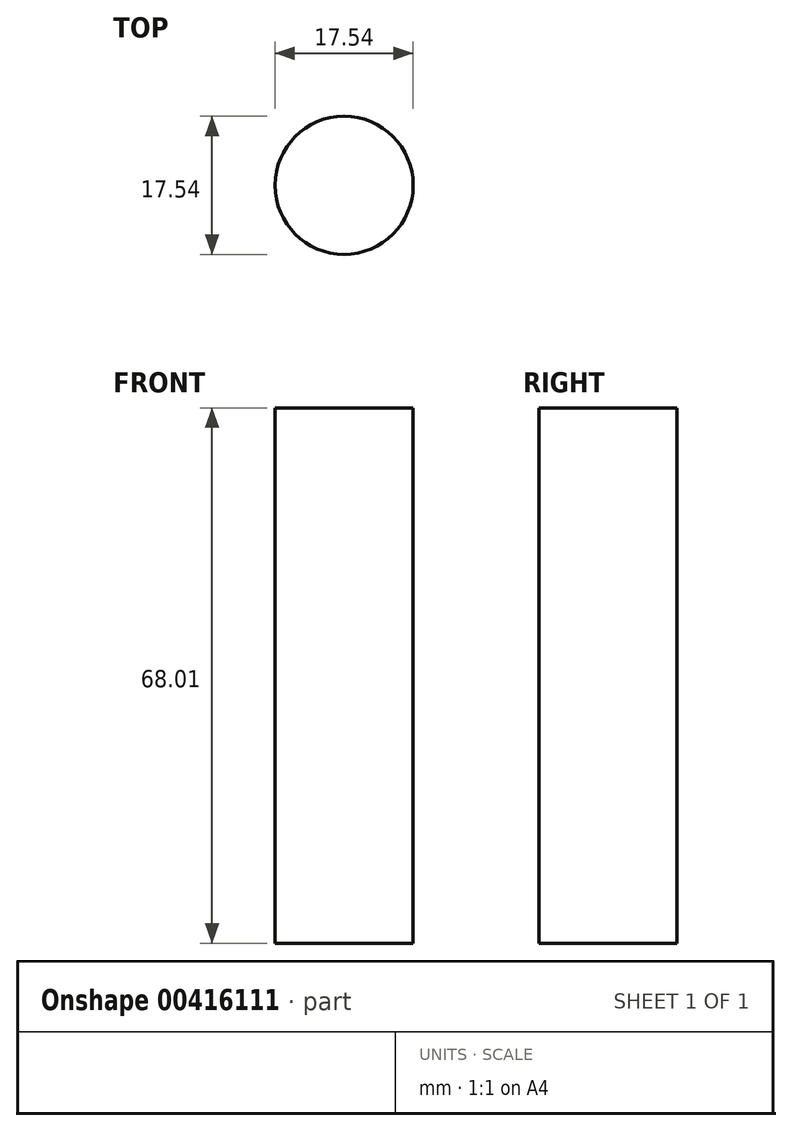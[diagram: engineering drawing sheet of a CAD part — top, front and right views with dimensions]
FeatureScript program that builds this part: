
annotation { "Feature Type Name" : "Feature", "Feature Type Description" : "" }
export const myFeature = defineFeature(function(context is Context, id is Id, definition is map)
    precondition{}
    {
        {
            var Q0;
            Q0=qCreatedBy(makeId("Front.planeOp"),FACE);
            var sketch = newSketch(context, id + "F0", { "sketchPlane" : qUnion([Q0])});
            skLineSegment(sketch, "E0", {"start": v(0, -81.86) * mm, "end": v(0, 103.76) * mm, "construction": true});
            skSolve(sketch);
        }
        {
            var Q0;
            Q0=qCreatedBy(makeId("Front.planeOp"),FACE);
            var sketch = newSketch(context, id + "F1", { "sketchPlane" : qUnion([Q0])});
            skLineSegment(sketch, "E1", {"start": v(0, 74.16) * mm, "end": v(-8.77, 74.16) * mm});
            skLineSegment(sketch, "E2", {"start": v(-8.77, 74.16) * mm, "end": v(-8.77, 6.15) * mm});
            skLineSegment(sketch, "E3", {"start": v(-8.77, 6.15) * mm, "end": v(0, 6.15) * mm});
            skLineSegment(sketch, "E4", {"start": v(0, 6.15) * mm, "end": v(0, 74.16) * mm});
            skSolve(sketch);
        }
        {
            var Q0;
            Q0=makeQuery(id+"F1.imprint","IMPRINT",FACE,{"disambiguationData":[TD([[makeQuery(id+"F1.imprint","IMPRINT",EDGE,{"derivedFrom":sQuery(id+"F1.wireOp",EDGE,"E1")}),1.0]])]});
            var Q1;
            Q1=sQuery(id+"F0.wireOp",EDGE,"E0");
            revolve(context, id + "F2", {"entities" : qUnion([Q0]), "axis" : qUnion([Q1]), "revolveType" : RevolveType.FULL});
        }
    });
